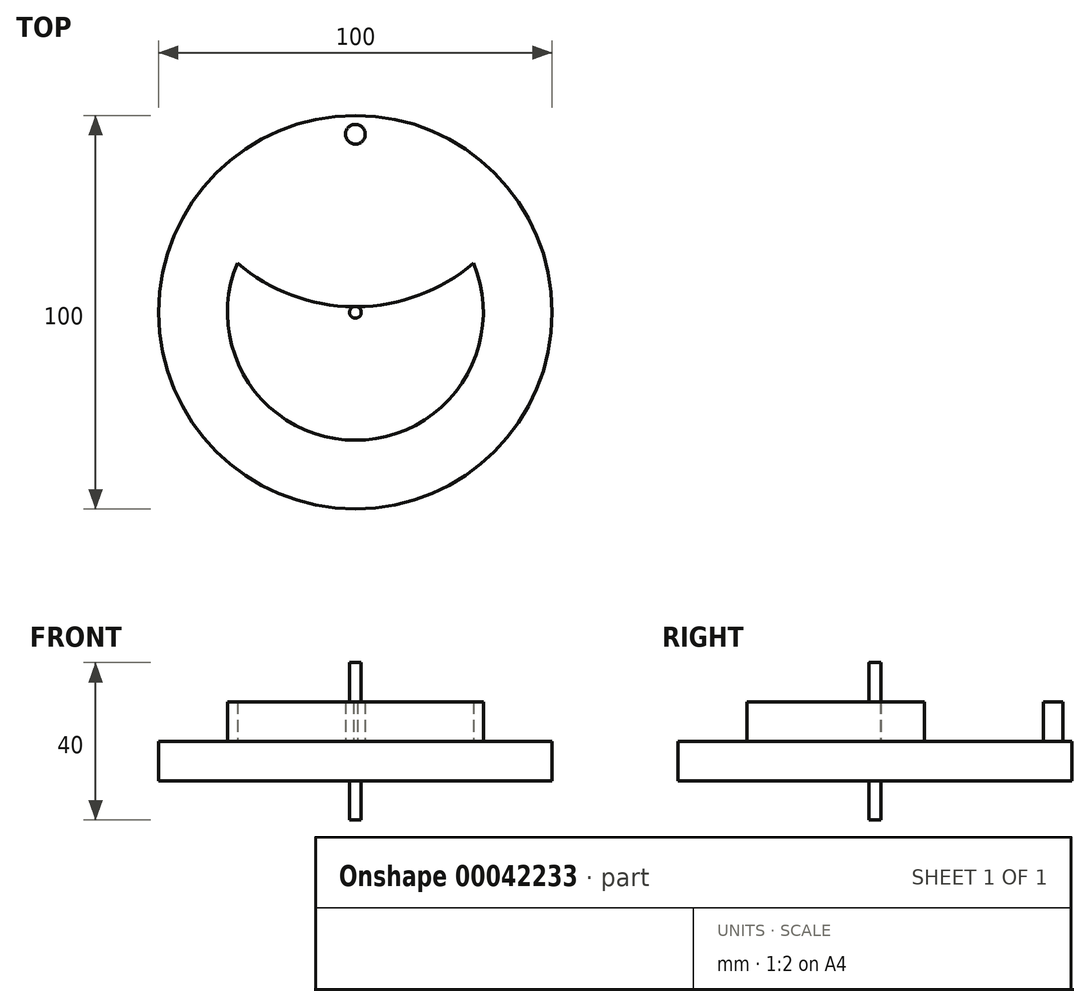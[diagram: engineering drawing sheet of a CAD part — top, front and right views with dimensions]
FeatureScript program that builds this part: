
annotation { "Feature Type Name" : "Feature", "Feature Type Description" : "" }
export const myFeature = defineFeature(function(context is Context, id is Id, definition is map)
    precondition{}
    {
        {
            var Q0;
            Q0=qCreatedBy(makeId("Top.planeOp"),FACE);
            var sketch = newSketch(context, id + "F0", { "sketchPlane" : qUnion([Q0])});
            skCircle(sketch, "E0", {"center": v(0, 0) * mm, "radius": 50 * mm});
            skSolve(sketch);
        }
        {
            var Q0;
            Q0=makeQuery(id+"F0.imprint","IMPRINT",FACE,{"disambiguationData":[TD([[makeQuery(id+"F0.imprint","IMPRINT",EDGE,{"derivedFrom":sQuery(id+"F0.wireOp",EDGE,"E0")}),1.0]])]});
            extrude(context, id + "F1", {"entities" : qUnion([Q0]), "depth" : 10 * mm});
        }
        {
            var Q0;
            Q0=makeQuery(id+"F1.opExtrude","CAP_FACE",FACE,{"disambiguationData":[OSD([sQuery(id+"F0.wireOp",EDGE,"E0")])],"isStart":false});
            var sketch = newSketch(context, id + "F2", { "sketchPlane" : qUnion([Q0])});
            skCircle(sketch, "E1", {"center": v(0, 0) * mm, "radius": 32.5 * mm});
            skLineSegment(sketch, "E2", {"start": v(-30, 12.5) * mm, "end": v(30, 12.5) * mm, "construction": true});
            skArc(sketch, "E3", {"start": v(-30, 12.5) * mm, "mid": v(0, 1.42) * mm, "end": v(30, 12.5) * mm});
            skSolve(sketch);
        }
        {
            var Q0;
            {var subQ0=sQuery(id+"F2.wireOp",EDGE,"E3");Q0=makeQuery(id+"F2.imprint","IMPRINT",FACE,{"disambiguationData":[TD([[makeQuery(id+"F2.imprint","IMPRINT",EDGE,{"derivedFrom":subQ0}),-1.0]])]});}
            extrude(context, id + "F3", {"entities" : qUnion([Q0]), "operationType" : NewBodyOperationType.ADD, "depth" : 10 * mm});
        }
        {
            var Q0;
            Q0=makeQuery(id+"F3.opExtrude","CAP_FACE",FACE,{"disambiguationData":[OSD([sQuery(id+"F2.wireOp",EDGE,"E1"),sQuery(id+"F2.wireOp",EDGE,"E3")])],"isStart":false});
            var sketch = newSketch(context, id + "F4", { "sketchPlane" : qUnion([Q0])});
            skCircle(sketch, "E4", {"center": v(0, 0) * mm, "radius": 1.5 * mm});
            skSolve(sketch);
        }
        {
            var Q0;
            Q0=makeQuery(id+"F4.imprint","IMPRINT",FACE,{"disambiguationData":[TD([[makeQuery(id+"F4.imprint","IMPRINT",EDGE,{"derivedFrom":sQuery(id+"F4.wireOp",EDGE,"E4")}),1.0]])]});
            var Q1;
            Q1=sQuery(id+"F4.wireOp",EDGE,"E4");
            extrude(context, id + "F5", {"entities" : qUnion([Q0]), "operationType" : NewBodyOperationType.ADD, "surfaceEntities" : qUnion([Q1]), "depth" : 10 * mm, "hasSecondDirection" : true, "secondDirectionOppositeDirection" : true, "secondDirectionDepth" : 30 * mm});
        }
        {
            var Q0;
            Q0=makeQuery(id+"F1.opExtrude","CAP_FACE",FACE,{"disambiguationData":[OSD([sQuery(id+"F0.wireOp",EDGE,"E0")])],"isStart":false});
            var sketch = newSketch(context, id + "F6", { "sketchPlane" : qUnion([Q0])});
            skPoint(sketch, "E5.endSnap0", {"position": v(-16.22, 4.36) * mm});
            skPoint(sketch, "E6.endSnap0", {"position": v(0, -32.5) * mm});
            skLineSegment(sketch, "E7", {"start": v(0, 0) * mm, "end": v(0, 25) * mm});
            skSolve(sketch);
        }
        {
            var Q0;
            Q0=makeQuery(id+"F6.imprint","IMPRINT",FACE,{"disambiguationData":[TD([[makeQuery(id+"F6.imprint","IMPRINT",EDGE,{"derivedFrom":makeQuery(id+"F1.opExtrude","CAP_EDGE",EDGE,{"disambiguationData":[OSD([sQuery(id+"F0.wireOp",EDGE,"E0")])],"isStart":false})}),1.0]])]});
            var sketch = newSketch(context, id + "F7", { "sketchPlane" : qUnion([Q0])});
            skCircle(sketch, "E8", {"center": v(0, 45.23) * mm, "radius": 2.5 * mm});
            skSolve(sketch);
        }
        {
            var Q0;
            Q0=makeQuery(id+"F7.imprint","IMPRINT",FACE,{"disambiguationData":[TD([[makeQuery(id+"F7.imprint","IMPRINT",EDGE,{"derivedFrom":sQuery(id+"F7.wireOp",EDGE,"E8")}),1.0]])]});
            var Q1;
            Q1=sQuery(id+"F7.wireOp",EDGE,"E8");
            extrude(context, id + "F8", {"entities" : qUnion([Q0]), "operationType" : NewBodyOperationType.ADD, "surfaceEntities" : qUnion([Q1]), "depth" : 10 * mm});
        }
    });
